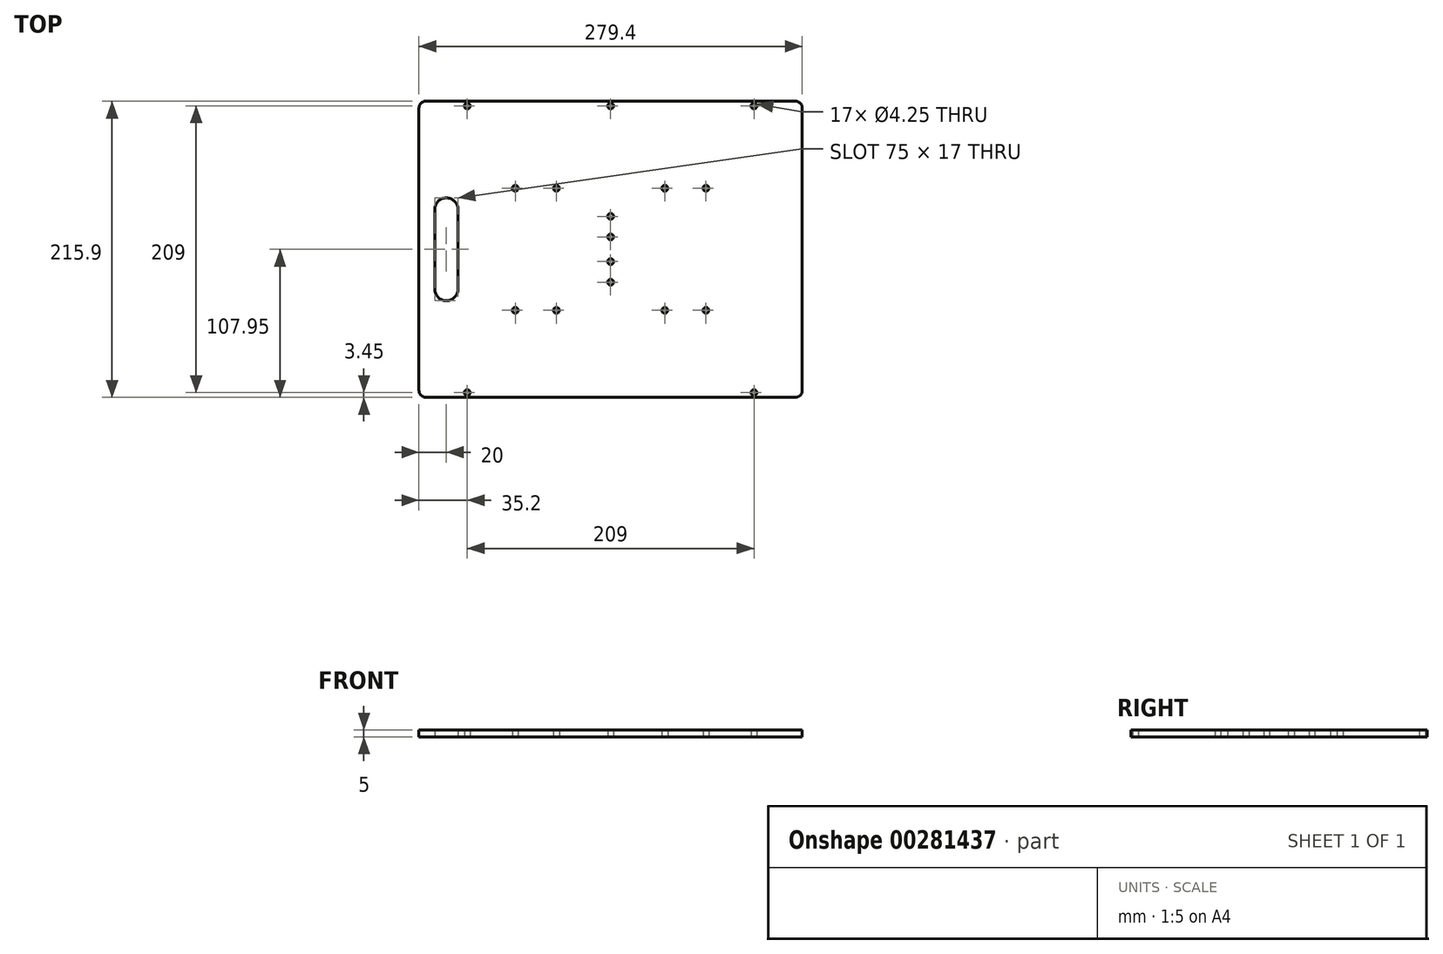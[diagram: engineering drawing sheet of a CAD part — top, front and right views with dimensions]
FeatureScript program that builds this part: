
annotation { "Feature Type Name" : "Feature", "Feature Type Description" : "" }
export const myFeature = defineFeature(function(context is Context, id is Id, definition is map)
    precondition{}
    {
        {
            var Q0;
            Q0=qCreatedBy(makeId("Top.planeOp"),FACE);
            var sketch = newSketch(context, id + "F0", { "sketchPlane" : qUnion([Q0])});
            skLineSegment(sketch, "E0.bottom", {"start": v(134.7, -107.95) * mm, "end": v(-134.7, -107.95) * mm});
            skLineSegment(sketch, "E0.top", {"start": v(134.7, 107.95) * mm, "end": v(-134.7, 107.95) * mm});
            skLineSegment(sketch, "E0.left", {"start": v(139.7, -102.95) * mm, "end": v(139.7, 0) * mm});
            skLineSegment(sketch, "E0.right", {"start": v(-139.7, -102.95) * mm, "end": v(-139.7, 0) * mm});
            skPoint(sketch, "E0.middle", {"position": v(0, 0) * mm});
            skPoint(sketch, "E1.visualSharp", {"position": v(-139.7, 107.95) * mm});
            skArc(sketch, "E1.filletArc", {"start": v(-134.7, 107.95) * mm, "mid": v(-138.24, 106.49) * mm, "end": v(-139.7, 102.95) * mm});
            skPoint(sketch, "E2.visualSharp", {"position": v(-139.7, -107.95) * mm});
            skArc(sketch, "E2.filletArc", {"start": v(-139.7, -102.95) * mm, "mid": v(-138.24, -106.49) * mm, "end": v(-134.7, -107.95) * mm});
            skPoint(sketch, "E3.visualSharp", {"position": v(139.7, -107.95) * mm});
            skArc(sketch, "E3.filletArc", {"start": v(134.7, -107.95) * mm, "mid": v(138.24, -106.49) * mm, "end": v(139.7, -102.95) * mm});
            skPoint(sketch, "E4.visualSharp", {"position": v(139.7, 107.95) * mm});
            skArc(sketch, "E4.filletArc", {"start": v(139.7, 102.95) * mm, "mid": v(138.24, 106.49) * mm, "end": v(134.7, 107.95) * mm});
            skLineSegment(sketch, "E5.trimOffspring", {"start": v(-139.7, 0) * mm, "end": v(-139.7, 102.95) * mm});
            skLineSegment(sketch, "E6.trimOffspring", {"start": v(139.7, 0) * mm, "end": v(139.7, 102.95) * mm});
            skLineSegment(sketch, "E7.bottom", {"start": v(119.7, 37.5) * mm, "end": v(119.7, 37.5) * mm});
            skLineSegment(sketch, "E7.top", {"start": v(119.7, -37.5) * mm, "end": v(119.7, -37.5) * mm});
            skLineSegment(sketch, "E7.left", {"start": v(128.2, 29) * mm, "end": v(128.2, -29) * mm, "construction": true});
            skLineSegment(sketch, "E7.right", {"start": v(111.2, 29) * mm, "end": v(111.2, -29) * mm, "construction": true});
            skPoint(sketch, "E7.middle", {"position": v(119.7, 0) * mm});
            skPoint(sketch, "E8.visualSharp", {"position": v(111.2, 37.5) * mm});
            skArc(sketch, "E8.filletArc", {"start": v(119.7, 37.5) * mm, "mid": v(113.69, 35.01) * mm, "end": v(111.2, 29) * mm, "construction": true});
            skPoint(sketch, "E9.visualSharp", {"position": v(128.2, 37.5) * mm});
            skArc(sketch, "E9.filletArc", {"start": v(128.2, 29) * mm, "mid": v(125.71, 35.01) * mm, "end": v(119.7, 37.5) * mm, "construction": true});
            skPoint(sketch, "E10.visualSharp", {"position": v(128.2, -37.5) * mm});
            skArc(sketch, "E10.filletArc", {"start": v(119.7, -37.5) * mm, "mid": v(125.71, -35.01) * mm, "end": v(128.2, -29) * mm, "construction": true});
            skPoint(sketch, "E11.visualSharp", {"position": v(111.2, -37.5) * mm});
            skArc(sketch, "E11.filletArc", {"start": v(111.2, -29) * mm, "mid": v(113.69, -35.01) * mm, "end": v(119.7, -37.5) * mm, "construction": true});
            skLineSegment(sketch, "E12", {"start": v(114.8, 107.95) * mm, "end": v(114.8, -107.95) * mm, "construction": true});
            skCircle(sketch, "E13", {"center": v(-104.5, 104.5) * mm, "radius": 2.12 * mm});
            skCircle(sketch, "E14", {"center": v(104.5, 104.5) * mm, "radius": 2.12 * mm});
            skCircle(sketch, "E15", {"center": v(-104.5, -104.5) * mm, "radius": 2.12 * mm});
            skCircle(sketch, "E16", {"center": v(104.5, -104.5) * mm, "radius": 2.12 * mm});
            skCircle(sketch, "E17", {"center": v(0, 104.5) * mm, "radius": 2.12 * mm});
            skPoint(sketch, "E18.centerSnap0", {"position": v(111.2, 0) * mm});
            skLineSegment(sketch, "E19.MirrorCS", {"start": v(-111.2, 29) * mm, "end": v(-111.2, -29) * mm});
            skArc(sketch, "E20.MirrorCS", {"start": v(-111.2, -29) * mm, "mid": v(-113.69, -35.01) * mm, "end": v(-119.7, -37.5) * mm});
            skArc(sketch, "E21.MirrorCS", {"start": v(-119.7, -37.5) * mm, "mid": v(-125.71, -35.01) * mm, "end": v(-128.2, -29) * mm});
            skLineSegment(sketch, "E22.MirrorCS", {"start": v(-128.2, 29) * mm, "end": v(-128.2, -29) * mm});
            skArc(sketch, "E23.MirrorCS", {"start": v(-128.2, 29) * mm, "mid": v(-125.71, 35.01) * mm, "end": v(-119.7, 37.5) * mm});
            skArc(sketch, "E24.MirrorCS", {"start": v(-119.7, 37.5) * mm, "mid": v(-113.69, 35.01) * mm, "end": v(-111.2, 29) * mm});
            skLineSegment(sketch, "E25.bottom", {"start": v(104.5, -104.5) * mm, "end": v(-104.5, -104.5) * mm, "construction": true});
            skLineSegment(sketch, "E25.top", {"start": v(104.5, 104.5) * mm, "end": v(-104.5, 104.5) * mm, "construction": true});
            skLineSegment(sketch, "E25.left", {"start": v(104.5, -104.5) * mm, "end": v(104.5, 104.5) * mm, "construction": true});
            skLineSegment(sketch, "E25.right", {"start": v(-104.5, -104.5) * mm, "end": v(-104.5, 104.5) * mm, "construction": true});
            skLineSegment(sketch, "E26.bottom", {"start": v(5, -29) * mm, "end": v(-5, -29) * mm, "construction": true});
            skLineSegment(sketch, "E26.top", {"start": v(5, 29) * mm, "end": v(-5, 29) * mm, "construction": true});
            skLineSegment(sketch, "E26.left", {"start": v(5, -29) * mm, "end": v(5, 29) * mm, "construction": true});
            skLineSegment(sketch, "E26.right", {"start": v(-5, -29) * mm, "end": v(-5, 29) * mm, "construction": true});
            skCircle(sketch, "E27", {"center": v(0, 24) * mm, "radius": 2.12 * mm});
            skCircle(sketch, "E28", {"center": v(0, 9) * mm, "radius": 2.12 * mm});
            skCircle(sketch, "E29", {"center": v(0, -9) * mm, "radius": 2.12 * mm});
            skCircle(sketch, "E30", {"center": v(0, -24) * mm, "radius": 2.12 * mm});
            skLineSegment(sketch, "E31.bottom", {"start": v(54.5, -54.5) * mm, "end": v(-54.5, -54.5) * mm, "construction": true});
            skLineSegment(sketch, "E31.top", {"start": v(54.5, 54.5) * mm, "end": v(-54.5, 54.5) * mm, "construction": true});
            skLineSegment(sketch, "E31.left", {"start": v(54.5, -54.5) * mm, "end": v(54.5, 54.5) * mm, "construction": true});
            skLineSegment(sketch, "E31.right", {"start": v(-54.5, -54.5) * mm, "end": v(-54.5, 54.5) * mm, "construction": true});
            skCircle(sketch, "E32", {"center": v(-69.5, 44.5) * mm, "radius": 2.12 * mm});
            skCircle(sketch, "E33", {"center": v(-39.5, 44.5) * mm, "radius": 2.12 * mm});
            skCircle(sketch, "E34.MirrorC", {"center": v(69.5, 44.5) * mm, "radius": 2.12 * mm});
            skCircle(sketch, "E35.MirrorC", {"center": v(39.5, 44.5) * mm, "radius": 2.12 * mm});
            skCircle(sketch, "E36.MirrorC", {"center": v(-69.5, -44.5) * mm, "radius": 2.12 * mm});
            skCircle(sketch, "E37.MirrorC", {"center": v(-39.5, -44.5) * mm, "radius": 2.12 * mm});
            skCircle(sketch, "E38.MirrorC", {"center": v(39.5, -44.5) * mm, "radius": 2.12 * mm});
            skCircle(sketch, "E39.MirrorC", {"center": v(69.5, -44.5) * mm, "radius": 2.12 * mm});
            skSolve(sketch);
        }
        {
            var Q0;
            Q0=qSketchRegion(id+"F0",true);
            extrude(context, id + "F1", {"entities" : qUnion([Q0]), "endBound" : BoundingType.SYMMETRIC, "depth" : 5 * mm});
        }
    });
